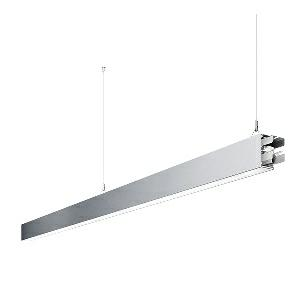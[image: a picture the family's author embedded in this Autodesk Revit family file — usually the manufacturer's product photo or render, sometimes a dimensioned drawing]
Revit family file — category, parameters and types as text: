
# Revit family: dotoo_line_-_dlp_3000_840_d_mid_00805831_f76e
name_source: partatom
category: Lighting Fixtures
units: mm (PartAtom-declared; Revit-internal decimal feet)

## family parameters
Cut with Voids When Loaded = No
Host = Face
Light Source = No
Part Type = Normal
Room Calculation Point = No
Round Connector Dimension = Use Diameter
Shared = No

## types (1)
- DOTOO.line - DLP 3000/840/D MID (1 x LED, 2750 lm, 4000K)
    Apparent Load = 26 VA
    Approval mark = CE
    CIE Flux Codes = 67 91 98 100 100
    Color Rendering = 80-89
    Color Temperature = 4000K
    Control Gear = Electronic ballast
    Default Elevation = 1800 mm
    Description = DLP 3000/840/D|Suspended luminaire|light source: LED|connected load: 220-240 V, 50/60 Hz|Power consumption: approx. 26 W|standby: approx. 0,15|luminous flux: 2750 lm|luminous efficacy: 105 lm/W|light distribution: Direct|direct ratio: approx. 100 %|colour temperature: Cold white, ca. 4000 K|color rendering index (CRI): >= 80|chromaticity tolerance:  3 SDCM|System of protection: IP 40|technology: Continuously dimmable|luminaire body|material: Sectional aluminium|colour: Silver|lamp cover: Acrylic (PMMA), Clear|mains lead: 1,0 m With free stranded wires|Fastening: Steel cable 0.3 - 0.7 m|glare control: Prism aperture|luminance(L65): <= 3000 cd/m|unified glare rating(4H 8H): <=  19|special features: DALI Load 1x, TouchDIM - dimming via standard switch, Through-wired, up to 18 m on one mains connection, Flicker-free, Suitable as emergency lighting, Mechanical and electrical connection of the individual modules without tools|
    Frequency = 50 Hz
    Height = 110 mm
    Lamp = 1 x LED
    Lamp Light Flux = 2750 lm
    Lamp count = 1
    Length = 2244 mm
    Luminous efficacy = 106 lm/W
    Manufacturer = Waldmann
    ModVariant = No
    Model = 00805831
    Mounting Place = Ceiling
    Mounting Type = Pendant
    Number of Poles = 1
    OnlyDefault = Yes
    Power Factor = 1
    Product Name = DOTOO.line - DLP 3000/840/D MID
    Product group = Suspended luminaire
    ProductGroupID = 9
    Protection Class = Protection class I
    Protection Degree = IP 40
    RLX_Detail_Level = 1
    RLX_Emergency_Light_Flux = 0 lm
    RLX_Emergency_Type = 0
    RLX_Emergency_Type_DB = No
    RlxData = <blob elided: 24225 chars, md5=df7127ca>
    Socket = socket
    Standby Power = 0 W
    System Light Flux = 2750 lm
    System Power = 26 W
    Type Comments = Product without accessories
    Type Image = 113317000-00692618.jpg
    URL = http://relux.com
    VarID = ---
    Voltage = 230 V
    Voltage Range = 220-240 V
    Weight = 0.00 kg
    Width = 60 mm  [stored 0.19685 ft]

note: [stored X ft] marks values corroborated as IEEE doubles in the binary element streams (Revit-internal decimal feet)

## geometry (parser evidence)
native form markers: Blend x4, Sweep x13
no freeform markers — native parametric forms only
